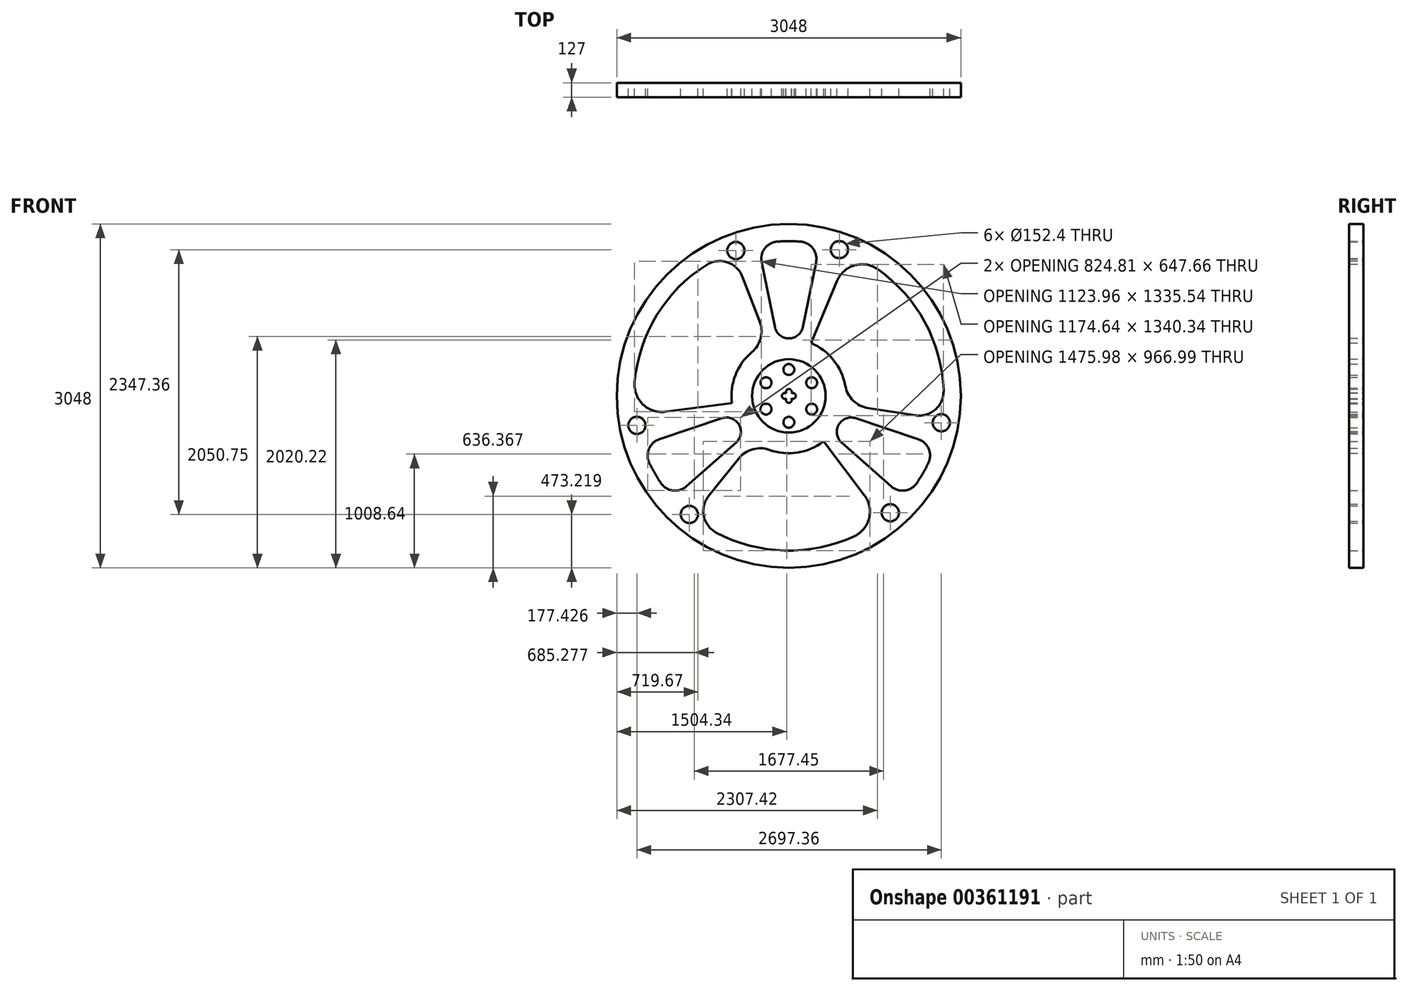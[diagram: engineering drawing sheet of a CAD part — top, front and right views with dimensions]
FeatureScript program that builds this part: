
annotation { "Feature Type Name" : "Feature", "Feature Type Description" : "" }
export const myFeature = defineFeature(function(context is Context, id is Id, definition is map)
    precondition{}
    {
        {
            var Q0;
            Q0=qCreatedBy(makeId("Front.planeOp"),FACE);
            var sketch = newSketch(context, id + "F0", { "sketchPlane" : qUnion([Q0])});
            skCircle(sketch, "E0", {"center": v(0, 0) * mm, "radius": 1524 * mm});
            skArc(sketch, "E1", {"start": v(-273.45, 1344.06) * mm, "mid": v(-1333.12, 322.6) * mm, "end": v(-857.71, -1070.34) * mm});
            skLineSegment(sketch, "E2", {"start": v(-124.45, 611.7) * mm, "end": v(-241.16, 1185.35) * mm});
            skLineSegment(sketch, "E3", {"start": v(124.45, 611.7) * mm, "end": v(241.16, 1185.35) * mm});
            skArc(sketch, "E4", {"start": v(-103.3, 1367.7) * mm, "mid": v(-213.39, 1307.65) * mm, "end": v(-241.16, 1185.35) * mm});
            skArc(sketch, "E5", {"start": v(241.16, 1185.35) * mm, "mid": v(213.39, 1307.65) * mm, "end": v(103.3, 1367.7) * mm});
            skArc(sketch, "E6.trimOffspring", {"start": v(103.3, 1367.7) * mm, "mid": v(0, 1371.6) * mm, "end": v(-103.3, 1367.7) * mm});
            skArc(sketch, "E7", {"start": v(-124.45, 611.7) * mm, "mid": v(0, 510.01) * mm, "end": v(124.45, 611.7) * mm});
            skLineSegment(sketch, "E8", {"start": v(0, 0) * mm, "end": v(-27.36, -2217.66) * mm});
            skPoint(sketch, "E8.endSnap0", {"position": v(-27.36, -1371.33) * mm});
            skLineSegment(sketch, "E9", {"start": v(0, 0) * mm, "end": v(669.04, -878.45) * mm});
            skLineSegment(sketch, "E10", {"start": v(0, 0) * mm, "end": v(-317.67, -396.42) * mm});
            skArc(sketch, "E11", {"start": v(-710.37, -886.47) * mm, "mid": v(-753.23, -1064.69) * mm, "end": v(-643.31, -1211.38) * mm});
            skArc(sketch, "E12", {"start": v(578.9, -1243.44) * mm, "mid": v(711.34, -1082.52) * mm, "end": v(669.04, -878.45) * mm});
            skLineSegment(sketch, "E13.trimOffspring", {"start": v(-857.71, -1070.34) * mm, "end": v(-1442.84, -1800.52) * mm});
            skArc(sketch, "E14.trimOffspring", {"start": v(-643.31, -1211.38) * mm, "mid": v(-35.97, -1371.13) * mm, "end": v(578.9, -1243.44) * mm});
            skArc(sketch, "E15.trimOffspring", {"start": v(831.04, -1091.17) * mm, "mid": v(1342.84, 279.4) * mm, "end": v(326.85, 1332.09) * mm});
            skLineSegment(sketch, "E16.trimOffspring", {"start": v(831.04, -1091.17) * mm, "end": v(1441.7, -1892.97) * mm});
            skCircle(sketch, "E17", {"center": v(0, 0) * mm, "radius": 508 * mm});
            skArc(sketch, "E18.1.0", {"start": v(-1132.82, -773.31) * mm, "mid": v(-1025.76, -838.62) * mm, "end": v(-905.96, -801.53) * mm});
            skArc(sketch, "E18.1.1", {"start": v(-1147.13, -383.82) * mm, "mid": v(-1239.15, -469.02) * mm, "end": v(-1236.12, -594.4) * mm});
            skLineSegment(sketch, "E18.1.2", {"start": v(-591.97, -198.07) * mm, "end": v(-1147.13, -383.82) * mm});
            skLineSegment(sketch, "E18.1.3", {"start": v(-467.52, -413.62) * mm, "end": v(-905.96, -801.53) * mm});
            skArc(sketch, "E18.1.4", {"start": v(-467.52, -413.62) * mm, "mid": v(-441.68, -255) * mm, "end": v(-591.97, -198.07) * mm});
            skArc(sketch, "E18.2.0", {"start": v(1236.12, -594.4) * mm, "mid": v(1239.15, -469.02) * mm, "end": v(1147.13, -383.82) * mm});
            skArc(sketch, "E18.2.1", {"start": v(905.96, -801.53) * mm, "mid": v(1025.76, -838.62) * mm, "end": v(1132.82, -773.31) * mm});
            skLineSegment(sketch, "E18.2.2", {"start": v(467.52, -413.62) * mm, "end": v(905.96, -801.53) * mm});
            skLineSegment(sketch, "E18.2.3", {"start": v(591.97, -198.07) * mm, "end": v(1147.13, -383.82) * mm});
            skArc(sketch, "E18.2.4", {"start": v(591.97, -198.07) * mm, "mid": v(441.68, -255) * mm, "end": v(467.52, -413.62) * mm});
            skCircle(sketch, "E19", {"center": v(-469.22, 1288.84) * mm, "radius": 76.2 * mm});
            skCircle(sketch, "E20", {"center": v(447.41, 1296.58) * mm, "radius": 76.2 * mm});
            skCircle(sketch, "E21.1.0", {"center": v(-881.56, -1050.78) * mm, "radius": 76.2 * mm});
            skCircle(sketch, "E21.1.1", {"center": v(-1346.57, -260.82) * mm, "radius": 76.2 * mm});
            skCircle(sketch, "E21.2.0", {"center": v(1350.78, -238.06) * mm, "radius": 76.2 * mm});
            skCircle(sketch, "E21.2.1", {"center": v(899.16, -1035.76) * mm, "radius": 76.2 * mm});
            skArc(sketch, "E22", {"start": v(-171.3, -478.25) * mm, "mid": v(-320.74, -473.14) * mm, "end": v(-445.36, -555.76) * mm});
            skArc(sketch, "E23", {"start": v(431.51, -566.58) * mm, "mid": v(308.97, -480.9) * mm, "end": v(159.45, -482.33) * mm});
            skLineSegment(sketch, "E24.trimOffspring", {"start": v(-445.36, -555.76) * mm, "end": v(-710.37, -886.47) * mm});
            skArc(sketch, "E25.1.0", {"start": v(1370.74, 48.56) * mm, "mid": v(1205.42, 654.41) * mm, "end": v(787.4, 1123.07) * mm});
            skArc(sketch, "E25.1.1", {"start": v(1122.89, -171.96) * mm, "mid": v(1298.66, -119.97) * mm, "end": v(1370.74, 48.56) * mm});
            skLineSegment(sketch, "E25.1.2", {"start": v(703.98, -107.81) * mm, "end": v(1122.89, -171.96) * mm});
            skArc(sketch, "E25.1.3", {"start": v(499.82, 90.77) * mm, "mid": v(570.12, -41.2) * mm, "end": v(703.98, -107.81) * mm});
            skArc(sketch, "E25.1.5", {"start": v(274.92, 656.99) * mm, "mid": v(262, 508.03) * mm, "end": v(337.98, 379.25) * mm});
            skLineSegment(sketch, "E25.1.6", {"start": v(0, 0) * mm, "end": v(426.25, 1018.63) * mm});
            skArc(sketch, "E25.1.7", {"start": v(787.4, 1123.07) * mm, "mid": v(581.82, 1157.3) * mm, "end": v(426.25, 1018.63) * mm});
            skArc(sketch, "E25.2.0", {"start": v(-727.43, 1162.81) * mm, "mid": v(-1169.45, 716.72) * mm, "end": v(-1366.3, 120.37) * mm});
            skArc(sketch, "E25.2.1", {"start": v(-412.52, 1058.43) * mm, "mid": v(-545.43, 1184.66) * mm, "end": v(-727.43, 1162.81) * mm});
            skLineSegment(sketch, "E25.2.2", {"start": v(-258.62, 663.57) * mm, "end": v(-412.52, 1058.43) * mm});
            skArc(sketch, "E25.2.3", {"start": v(-328.52, 387.47) * mm, "mid": v(-249.38, 514.34) * mm, "end": v(-258.62, 663.57) * mm});
            skArc(sketch, "E25.2.5", {"start": v(-706.43, -90.4) * mm, "mid": v(-570.96, -27.12) * mm, "end": v(-497.43, 103.08) * mm});
            skLineSegment(sketch, "E25.2.6", {"start": v(0, 0) * mm, "end": v(-1095.28, -140.18) * mm});
            skArc(sketch, "E25.2.7", {"start": v(-1366.3, 120.37) * mm, "mid": v(-1293.16, -74.78) * mm, "end": v(-1095.28, -140.18) * mm});
            skSolve(sketch);
        }
        {
            var Q0;
            {var subQ0=sQuery(id+"F0.wireOp",EDGE,"E17");var subQ4=makeQuery(id+"F0.imprint","INTERSECT",VERTEX,{"derivedFrom":[sQuery(id+"F0.wireOp",EDGE,"E25.2.3"),subQ0]});Q0=makeQuery(id+"F0.imprint","IMPRINT",FACE,{"disambiguationData":[TD([[makeQuery(id+"F0.imprint","IMPRINT",EDGE,{"disambiguationData":[TD([[subQ4,1.0]])],"derivedFrom":subQ0}),1.0]])]});}
            var sketch = newSketch(context, id + "F1", { "sketchPlane" : qUnion([Q0])});
            skArc(sketch, "E26", {"start": v(-27.48, -23.8) * mm, "mid": v(-25.7, -25.7) * mm, "end": v(-23.8, -27.48) * mm});
            skCircle(sketch, "E27", {"center": v(0, 0) * mm, "radius": 325.38 * mm});
            skCircle(sketch, "E28", {"center": v(0, 233.8) * mm, "radius": 48.35 * mm});
            skCircle(sketch, "E29.1.3.0", {"center": v(0, -233.8) * mm, "radius": 48.35 * mm});
            skCircle(sketch, "E29.1.4.0", {"center": v(202.47, -116.9) * mm, "radius": 48.35 * mm});
            skCircle(sketch, "E29.1.5.0", {"center": v(202.47, 116.9) * mm, "radius": 48.35 * mm});
            skCircle(sketch, "E30.1.0", {"center": v(-202.47, 116.9) * mm, "radius": 48.35 * mm});
            skCircle(sketch, "E31.1.0", {"center": v(-202.47, -116.9) * mm, "radius": 48.35 * mm});
            skArc(sketch, "E32", {"start": v(-23.8, -27.48) * mm, "mid": v(0, -61.75) * mm, "end": v(23.8, -27.48) * mm});
            skArc(sketch, "E33", {"start": v(27.48, -23.8) * mm, "mid": v(61.75, 0) * mm, "end": v(27.48, 23.8) * mm});
            skArc(sketch, "E34", {"start": v(-27.48, 23.8) * mm, "mid": v(-61.75, 0) * mm, "end": v(-27.48, -23.8) * mm});
            skArc(sketch, "E35", {"start": v(23.8, 27.48) * mm, "mid": v(0, 61.75) * mm, "end": v(-23.8, 27.48) * mm});
            skArc(sketch, "E36.trimOffspring", {"start": v(23.8, -27.48) * mm, "mid": v(25.7, -25.7) * mm, "end": v(27.48, -23.8) * mm});
            skArc(sketch, "E37.trimOffspring", {"start": v(27.48, 23.8) * mm, "mid": v(25.7, 25.7) * mm, "end": v(23.8, 27.48) * mm});
            skArc(sketch, "E38.trimOffspring", {"start": v(-23.8, 27.48) * mm, "mid": v(-25.7, 25.7) * mm, "end": v(-27.48, 23.8) * mm});
            skSolve(sketch);
        }
        {
            var Q0;
            Q0=makeQuery(id+"F0.imprint","IMPRINT",FACE,{"disambiguationData":[TD([[makeQuery(id+"F0.imprint","IMPRINT",EDGE,{"derivedFrom":sQuery(id+"F0.wireOp",EDGE,"E2")}),1.0]])]});
            var Q1;
            {var subQ2=sQuery(id+"F0.wireOp",EDGE,"E11");Q1=makeQuery(id+"F0.imprint","IMPRINT",FACE,{"disambiguationData":[TD([[makeQuery(id+"F0.imprint","IMPRINT",EDGE,{"derivedFrom":subQ2}),-1.0]])]});}
            var Q2;
            {var subQ9=sQuery(id+"F0.wireOp",EDGE,"E12");Q2=makeQuery(id+"F0.imprint","IMPRINT",FACE,{"disambiguationData":[TD([[makeQuery(id+"F0.imprint","IMPRINT",EDGE,{"derivedFrom":subQ9}),-1.0]])]});}
            var Q3;
            {var subQ3=sQuery(id+"F0.wireOp",EDGE,"E17");var subQ6=makeQuery(id+"F0.imprint","INTERSECT",VERTEX,{"derivedFrom":[sQuery(id+"F0.wireOp",EDGE,"E23"),subQ3]});Q3=makeQuery(id+"F0.imprint","IMPRINT",FACE,{"disambiguationData":[TD([[makeQuery(id+"F0.imprint","IMPRINT",EDGE,{"disambiguationData":[TD([[subQ6,1.0]])],"derivedFrom":subQ3}),1.0]])]});}
            var Q4;
            {var subQ0=sQuery(id+"F0.wireOp",EDGE,"E10");Q4=makeQuery(id+"F0.imprint","IMPRINT",FACE,{"disambiguationData":[TD([[makeQuery(id+"F0.imprint","IMPRINT",EDGE,{"derivedFrom":subQ0}),1.0]])]});}
            var Q5;
            {var subQ0=sQuery(id+"F0.wireOp",EDGE,"E10");Q5=makeQuery(id+"F0.imprint","IMPRINT",FACE,{"disambiguationData":[TD([[makeQuery(id+"F0.imprint","IMPRINT",EDGE,{"derivedFrom":subQ0}),-1.0]])]});}
            var Q6;
            {var subQ1=sQuery(id+"F1.wireOp",EDGE,"E26");Q6=makeQuery(id+"F1.imprint","IMPRINT",FACE,{"disambiguationData":[TD([[makeQuery(id+"F1.imprint","IMPRINT",EDGE,{"derivedFrom":subQ1}),-1.0]])]});}
            var Q7;
            Q7=makeQuery(id+"F1.imprint","IMPRINT",FACE,{"disambiguationData":[TD([[makeQuery(id+"F1.imprint","IMPRINT",EDGE,{"derivedFrom":sQuery(id+"F1.wireOp",EDGE,"E28")}),-1.0]])]});
            var Q8;
            {var subQ0=sQuery(id+"F0.wireOp",EDGE,"E17");var subQ4=makeQuery(id+"F0.imprint","INTERSECT",VERTEX,{"derivedFrom":[sQuery(id+"F0.wireOp",EDGE,"E25.2.3"),subQ0]});Q8=makeQuery(id+"F0.imprint","IMPRINT",FACE,{"disambiguationData":[TD([[makeQuery(id+"F0.imprint","IMPRINT",EDGE,{"disambiguationData":[TD([[subQ4,1.0]])],"derivedFrom":subQ0}),1.0]])]});}
            var Q9;
            {var subQ0=sQuery(id+"F0.wireOp",EDGE,"E17");var subQ1=makeQuery(id+"F0.imprint","INTERSECT",VERTEX,{"derivedFrom":[sQuery(id+"F0.wireOp",EDGE,"E25.1.3"),subQ0]});Q9=makeQuery(id+"F0.imprint","IMPRINT",FACE,{"disambiguationData":[TD([[makeQuery(id+"F0.imprint","IMPRINT",EDGE,{"disambiguationData":[TD([[subQ1,1.0]])],"derivedFrom":subQ0}),1.0]])]});}
            extrude(context, id + "F2", {"entities" : qUnion([Q0, Q1, Q2, Q3, Q4, Q5, Q6, Q7, Q8, Q9]), "depth" : 127 * mm});
        }
    });
